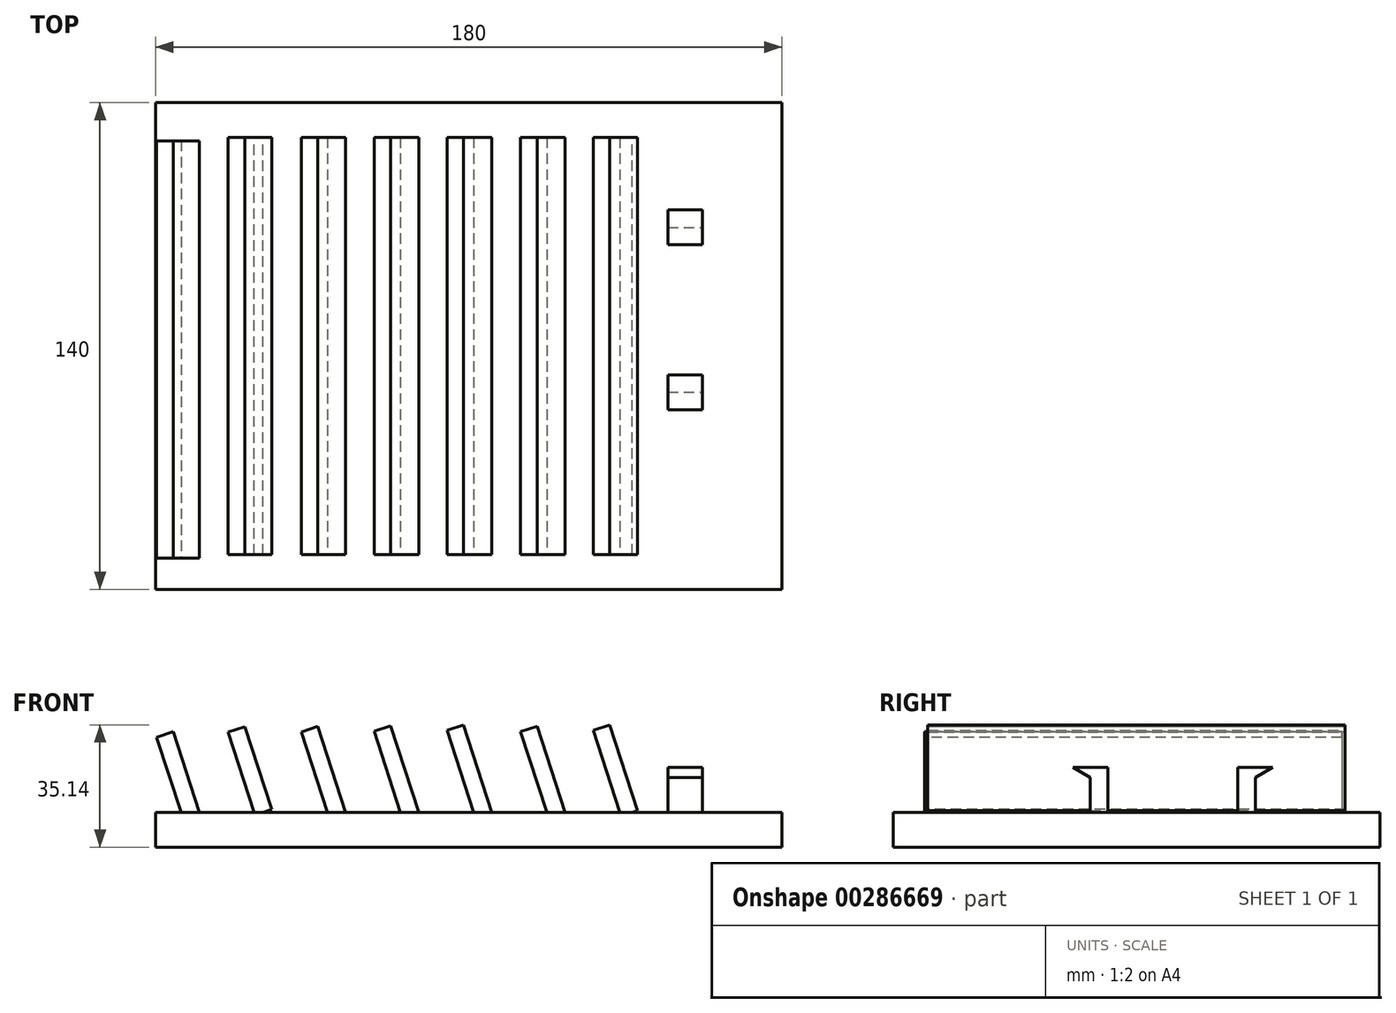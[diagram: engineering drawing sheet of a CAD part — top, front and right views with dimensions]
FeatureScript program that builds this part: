
annotation { "Feature Type Name" : "Feature", "Feature Type Description" : "" }
export const myFeature = defineFeature(function(context is Context, id is Id, definition is map)
    precondition{}
    {
        {
            var Q0;
            Q0=qCreatedBy(makeId("Top.planeOp"),FACE);
            var sketch = newSketch(context, id + "F0", { "sketchPlane" : qUnion([Q0])});
            skLineSegment(sketch, "E0.bottom", {"start": v(-90, 70) * mm, "end": v(90, 70) * mm});
            skLineSegment(sketch, "E0.top", {"start": v(-90, -70) * mm, "end": v(90, -70) * mm});
            skLineSegment(sketch, "E0.left", {"start": v(-90, 70) * mm, "end": v(-90, -70) * mm});
            skLineSegment(sketch, "E0.right", {"start": v(90, 70) * mm, "end": v(90, -70) * mm});
            skPoint(sketch, "E0.middle", {"position": v(0, 0) * mm});
            skSolve(sketch);
        }
        {
            var Q0;
            Q0=qCreatedBy(makeId("Top.planeOp"),FACE);
            var Q1;
            Q1=sQuery(id+"F0.wireOp",EDGE,"E0.left");
            cPlane(context, id + "F1", {"entities" : qUnion([Q0, Q1]), "cplaneType" : CPlaneType.LINE_ANGLE, "offset" : 25.4 * mm, "angle" : 18 * degree, "width" : 152.4 * mm, "height" : 152.4 * mm});
        }
        {
            var Q0;
            Q0=qCreatedBy(id+"F1.planeOp",FACE);
            var sketch = newSketch(context, id + "F2", { "sketchPlane" : qUnion([Q0])});
            skLineSegment(sketch, "E1.bottom", {"start": v(-75.6, -59.05) * mm, "end": v(-70.6, -59.05) * mm});
            skLineSegment(sketch, "E1.top", {"start": v(-75.6, 60.95) * mm, "end": v(-70.6, 60.95) * mm});
            skLineSegment(sketch, "E1.left", {"start": v(-75.6, -59.05) * mm, "end": v(-75.6, 60.95) * mm});
            skLineSegment(sketch, "E1.right", {"start": v(-70.6, -59.05) * mm, "end": v(-70.6, 60.95) * mm});
            skSolve(sketch);
        }
        {
            var Q0;
            Q0=makeQuery(id+"F2.imprint","IMPRINT",FACE,{"disambiguationData":[TD([[makeQuery(id+"F2.imprint","IMPRINT",EDGE,{"derivedFrom":sQuery(id+"F2.wireOp",EDGE,"E1.bottom")}),1.0]])]});
            extrude(context, id + "F3", {"entities" : qUnion([Q0]), "oppositeDirection" : true, "depth" : 30 * mm});
        }
        {
            var Q0;
            Q0 = qSketchRegion(id + "F0", true);
            extrude(context, id + "F4", {"entities" : qUnion([Q0]), "operationType" : NewBodyOperationType.ADD, "depth" : 10 * mm});
        }
        {
            var Q0;
            Q0=qCreatedBy(id+"F1.planeOp",FACE);
            var sketch = newSketch(context, id + "F5", { "sketchPlane" : qUnion([Q0])});
            skLineSegment(sketch, "E2.bottom", {"start": v(-55.6, -60) * mm, "end": v(-50.6, -60) * mm});
            skLineSegment(sketch, "E2.top", {"start": v(-55.6, 60) * mm, "end": v(-50.6, 60) * mm});
            skLineSegment(sketch, "E2.left", {"start": v(-55.6, -60) * mm, "end": v(-55.6, 60) * mm});
            skLineSegment(sketch, "E2.right", {"start": v(-50.6, -60) * mm, "end": v(-50.6, 60) * mm});
            skSolve(sketch);
        }
        {
            var Q0;
            Q0 = qSketchRegion(id + "F5", true);
            extrude(context, id + "F6", {"entities" : qUnion([Q0]), "operationType" : NewBodyOperationType.ADD, "oppositeDirection" : true, "depth" : 25 * mm});
        }
        {
            var Q0;
            Q0=makeQuery(id+"F4.opExtrude","CAP_FACE",FACE,{"disambiguationData":[OSD([sQuery(id+"F0.wireOp",EDGE,"E0.bottom"),sQuery(id+"F0.wireOp",EDGE,"E0.top"),sQuery(id+"F0.wireOp",EDGE,"E0.left"),sQuery(id+"F0.wireOp",EDGE,"E0.right")])],"isStart":false});
            var sketch = newSketch(context, id + "F7", { "sketchPlane" : qUnion([Q0])});
            skLineSegment(sketch, "E3", {"start": v(-29.16, 74.56) * mm, "end": v(-29.16, -85.98) * mm, "construction": true});
            skLineSegment(sketch, "E4", {"start": v(9.52, 74.73) * mm, "end": v(9.52, -86.39) * mm, "construction": true});
            skLineSegment(sketch, "E5", {"start": v(46.99, 74.73) * mm, "end": v(46.99, -84.07) * mm, "construction": true});
            skSolve(sketch);
        }
        {
            var Q0;
            Q0=sQuery(id+"F7.wireOp",EDGE,"E3");
            cPlane(context, id + "F8", {"entities" : qUnion([Q0]), "cplaneType" : CPlaneType.LINE_ANGLE, "offset" : 25 * mm, "angle" : 18 * degree, "width" : 150 * mm, "height" : 150 * mm});
        }
        {
            var Q0;
            Q0=qCreatedBy(id+"F8.planeOp",FACE);
            var sketch = newSketch(context, id + "F9", { "sketchPlane" : qUnion([Q0])});
            skLineSegment(sketch, "E6.bottom", {"start": v(-35.6, 60) * mm, "end": v(-30.6, 60) * mm});
            skLineSegment(sketch, "E6.top", {"start": v(-35.6, -60) * mm, "end": v(-30.6, -60) * mm});
            skLineSegment(sketch, "E6.left", {"start": v(-35.6, 60) * mm, "end": v(-35.6, -60) * mm});
            skLineSegment(sketch, "E6.right", {"start": v(-30.6, 60) * mm, "end": v(-30.6, -60) * mm});
            skSolve(sketch);
        }
        {
            var Q0;
            Q0 = qSketchRegion(id + "F9", true);
            extrude(context, id + "F10", {"entities" : qUnion([Q0]), "operationType" : NewBodyOperationType.ADD, "oppositeDirection" : true, "depth" : 27.9 * mm});
        }
        {
            var Q0;
            Q0=sQuery(id+"F7.wireOp",EDGE,"E4");
            cPlane(context, id + "F11", {"entities" : qUnion([Q0]), "cplaneType" : CPlaneType.LINE_ANGLE, "offset" : 25 * mm, "angle" : 18 * degree, "width" : 150 * mm, "height" : 150 * mm});
        }
        {
            var Q0;
            Q0=qCreatedBy(id+"F11.planeOp",FACE);
            var sketch = newSketch(context, id + "F12", { "sketchPlane" : qUnion([Q0])});
            skLineSegment(sketch, "E7.bottom", {"start": v(-10.6, 60) * mm, "end": v(-15.6, 60) * mm});
            skLineSegment(sketch, "E7.top", {"start": v(-10.6, -60) * mm, "end": v(-15.6, -60) * mm});
            skLineSegment(sketch, "E7.left", {"start": v(-10.6, 60) * mm, "end": v(-10.6, -60) * mm});
            skLineSegment(sketch, "E7.right", {"start": v(-15.6, 60) * mm, "end": v(-15.6, -60) * mm});
            skSolve(sketch);
        }
        {
            var Q0;
            Q0 = qSketchRegion(id + "F12", true);
            extrude(context, id + "F13", {"entities" : qUnion([Q0]), "operationType" : NewBodyOperationType.ADD, "oppositeDirection" : true, "depth" : 33.6 * mm});
        }
        {
            var Q0;
            Q0=qCreatedBy(id+"F11.planeOp",FACE);
            var sketch = newSketch(context, id + "F14", { "sketchPlane" : qUnion([Q0])});
            skLineSegment(sketch, "E8.bottom", {"start": v(9.4, 60) * mm, "end": v(4.4, 60) * mm});
            skLineSegment(sketch, "E8.top", {"start": v(9.4, -60) * mm, "end": v(4.4, -60) * mm});
            skLineSegment(sketch, "E8.left", {"start": v(9.4, 60) * mm, "end": v(9.4, -60) * mm});
            skLineSegment(sketch, "E8.right", {"start": v(4.4, 60) * mm, "end": v(4.4, -60) * mm});
            skLineSegment(sketch, "E9.bottom", {"start": v(4.4, -60) * mm, "end": v(9.4, -60) * mm});
            skLineSegment(sketch, "E9.top", {"start": v(4.4, -60) * mm, "end": v(9.4, -60) * mm});
            skLineSegment(sketch, "E9.left", {"start": v(4.4, -60) * mm, "end": v(4.4, -60) * mm});
            skLineSegment(sketch, "E9.right", {"start": v(9.4, -60) * mm, "end": v(9.4, -60) * mm});
            skSolve(sketch);
        }
        {
            var Q0;
            Q0 = qSketchRegion(id + "F14", true);
            extrude(context, id + "F15", {"entities" : qUnion([Q0]), "operationType" : NewBodyOperationType.ADD, "oppositeDirection" : true, "depth" : 27.3 * mm});
        }
        {
            var Q0;
            Q0=sQuery(id+"F7.wireOp",EDGE,"E5");
            cPlane(context, id + "F16", {"entities" : qUnion([Q0]), "cplaneType" : CPlaneType.LINE_ANGLE, "offset" : 25 * mm, "angle" : 18 * degree, "width" : 150 * mm, "height" : 150 * mm});
        }
        {
            var Q0;
            Q0=qCreatedBy(id+"F16.planeOp",FACE);
            var sketch = newSketch(context, id + "F17", { "sketchPlane" : qUnion([Q0])});
            skLineSegment(sketch, "E10.bottom", {"start": v(29.4, 60) * mm, "end": v(24.4, 60) * mm});
            skLineSegment(sketch, "E10.top", {"start": v(29.4, -60) * mm, "end": v(24.4, -60) * mm});
            skLineSegment(sketch, "E10.left", {"start": v(29.4, 60) * mm, "end": v(29.4, -60) * mm});
            skLineSegment(sketch, "E10.right", {"start": v(24.4, 60) * mm, "end": v(24.4, -60) * mm});
            skSolve(sketch);
        }
        {
            var Q0;
            Q0 = qSketchRegion(id + "F17", true);
            extrude(context, id + "F18", {"entities" : qUnion([Q0]), "operationType" : NewBodyOperationType.ADD, "oppositeDirection" : true, "depth" : 32 * mm});
        }
        {
            var Q0;
            Q0=qCreatedBy(id+"F16.planeOp",FACE);
            var sketch = newSketch(context, id + "F19", { "sketchPlane" : qUnion([Q0])});
            skLineSegment(sketch, "E11.bottom", {"start": v(49.4, 60) * mm, "end": v(44.4, 60) * mm});
            skLineSegment(sketch, "E11.top", {"start": v(49.4, -60) * mm, "end": v(44.4, -60) * mm});
            skLineSegment(sketch, "E11.left", {"start": v(49.4, 60) * mm, "end": v(49.4, -60) * mm});
            skLineSegment(sketch, "E11.right", {"start": v(44.4, 60) * mm, "end": v(44.4, -60) * mm});
            skSolve(sketch);
        }
        {
            var Q0;
            Q0 = qSketchRegion(id + "F19", true);
            extrude(context, id + "F20", {"entities" : qUnion([Q0]), "operationType" : NewBodyOperationType.ADD, "oppositeDirection" : true, "depth" : 25.9 * mm});
        }
        {
            var Q0;
            Q0=makeQuery(id+"F0.imprint","IMPRINT",FACE,{"disambiguationData":[TD([[makeQuery(id+"F0.imprint","IMPRINT",EDGE,{"derivedFrom":sQuery(id+"F0.wireOp",EDGE,"E0.bottom")}),-1.0]])]});
            cPlane(context, id + "F21", {"entities" : qUnion([Q0]), "cplaneType" : CPlaneType.OFFSET, "offset" : 10 * mm, "width" : 150 * mm, "height" : 150 * mm});
        }
        {
            var Q0;
            Q0=qCreatedBy(id+"F21.planeOp",FACE);
            var sketch = newSketch(context, id + "F22", { "sketchPlane" : qUnion([Q0])});
            skLineSegment(sketch, "E12", {"start": v(57.2, 39.15) * mm, "end": v(57.2, 29.15) * mm});
            skLineSegment(sketch, "E13", {"start": v(57.2, 29.15) * mm, "end": v(67.2, 29.15) * mm});
            skLineSegment(sketch, "E14", {"start": v(67.2, 29.15) * mm, "end": v(67.2, 39.15) * mm});
            skLineSegment(sketch, "E15", {"start": v(67.2, 39.15) * mm, "end": v(57.2, 39.15) * mm});
            skLineSegment(sketch, "E16", {"start": v(57.2, -8.28) * mm, "end": v(57.2, -18.28) * mm});
            skLineSegment(sketch, "E17", {"start": v(57.2, -18.28) * mm, "end": v(67.2, -18.28) * mm});
            skLineSegment(sketch, "E18", {"start": v(67.2, -18.28) * mm, "end": v(67.2, -8.28) * mm});
            skLineSegment(sketch, "E19", {"start": v(67.2, -8.28) * mm, "end": v(57.2, -8.28) * mm});
            skSolve(sketch);
        }
        {
            var Q0;
            Q0 = qSketchRegion(id + "F22", true);
            extrude(context, id + "F23", {"entities" : qUnion([Q0]), "operationType" : NewBodyOperationType.ADD, "depth" : 13 * mm});
        }
        {
            var Q0;
            Q0=makeQuery(id+"F23.opExtrude","SWEPT_FACE",FACE,{"disambiguationData":[OSD([sQuery(id+"F22.wireOp",EDGE,"E14")])]});
            var sketch = newSketch(context, id + "F24", { "sketchPlane" : qUnion([Q0])});
            skLineSegment(sketch, "E20", {"start": v(39.15, 23) * mm, "end": v(34.15, 20) * mm});
            skLineSegment(sketch, "E21", {"start": v(34.15, 20) * mm, "end": v(34.15, 10) * mm});
            skSolve(sketch);
        }
        {
            var Q0;
            Q0=makeQuery(id+"F23.opExtrude","SWEPT_FACE",FACE,{"disambiguationData":[OSD([sQuery(id+"F22.wireOp",EDGE,"E18")])]});
            var sketch = newSketch(context, id + "F25", { "sketchPlane" : qUnion([Q0])});
            skLineSegment(sketch, "E22", {"start": v(-18.28, 23) * mm, "end": v(-13.28, 20) * mm});
            skLineSegment(sketch, "E23", {"start": v(-13.28, 20) * mm, "end": v(-13.28, 10) * mm});
            skPoint(sketch, "E23.endSnap0", {"position": v(-13.28, 10) * mm});
            skSolve(sketch);
        }
        {
            var Q0;
            Q0=makeQuery(id+"F25.imprint","IMPRINT",FACE,{"disambiguationData":[TD([[makeQuery(id+"F25.imprint","IMPRINT",EDGE,{"derivedFrom":sQuery(id+"F25.wireOp",EDGE,"E22")}),-1.0]])]});
            var Q1;
            Q1=makeQuery(id+"F24.imprint","IMPRINT",FACE,{"disambiguationData":[TD([[makeQuery(id+"F24.imprint","IMPRINT",EDGE,{"derivedFrom":sQuery(id+"F24.wireOp",EDGE,"E20")}),1.0]])]});
            extrude(context, id + "F26", {"entities" : qUnion([Q0, Q1]), "operationType" : NewBodyOperationType.REMOVE, "oppositeDirection" : true, "depth" : 15 * mm});
        }
    });
